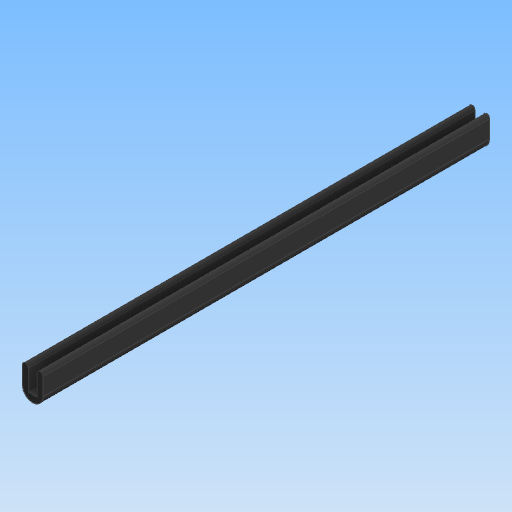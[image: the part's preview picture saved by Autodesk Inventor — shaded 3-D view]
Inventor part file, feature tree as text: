
AUTODESK INVENTOR PART (.ipt)
format: ipt  version: 2020 (Build 240168000, 168)  size: 104,448 bytes
history: native  units: mm
features: other x1, extrude x1
ambient origin geometry x8: Origin, YZ Plane, XZ Plane, XY Plane, X Axis, Y Axis, Z Axis, Center Point
bodies: Body1 (feature_tree)
feature tree (2):
  other  "實體1"
  extrude  "擠出1"  Depth=6.0mm
